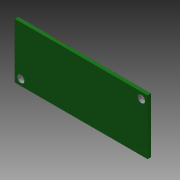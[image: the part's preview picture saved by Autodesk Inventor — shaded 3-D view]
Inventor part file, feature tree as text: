
AUTODESK INVENTOR PART (.ipt)
format: ipt  version: 2015 (Build 190159000, 159)  size: 148,480 bytes
history: native  units: mm
features: sketch x3, extrude x2, sweep x1, pattern_linear x1
ambient origin geometry x8: Origin, YZ Plane, XZ Plane, XY Plane, X Axis, Y Axis, Z Axis, Center Point
bodies: Solid1 (feature_tree)
feature tree (7):
  sketch  "Sketch1"  dims[d0=65.024mm d1=27.0mm]
  extrude  "Extrusion1"  Depth=27.0mm
  extrude  "Extrusion2"  Depth=3.5mm
  sweep  "Sweep1"
  pattern_linear  "Rectangular Pattern1"  Spacing1=3.0mm  [1 undecoded]
  sketch  "Sketch3"  dims[d4=3.0mm d5=3.0mm d6=3.0mm d7=3.0mm d8=9.96mm d9=11.66mm d10=1.0mm d11=1.27mm d12=3.937mm d13=1.7mm d14=0.0mm d15=8.62mm d16=0.0mm d17=6.15mm d18=90.0deg d19=7.87mm d20=90.0deg d21=0.0mm d22=0.0mm d23=180.0mm d25=2.54mm]
  sketch  "Sketch2"  dims[d2=3.5mm d3=3.5mm]
note: 1 required parameter value undecoded (feature->parameter linkage not recoverable at this tier; creation-order binding heuristic only, values carry confidence <= 0.55)
